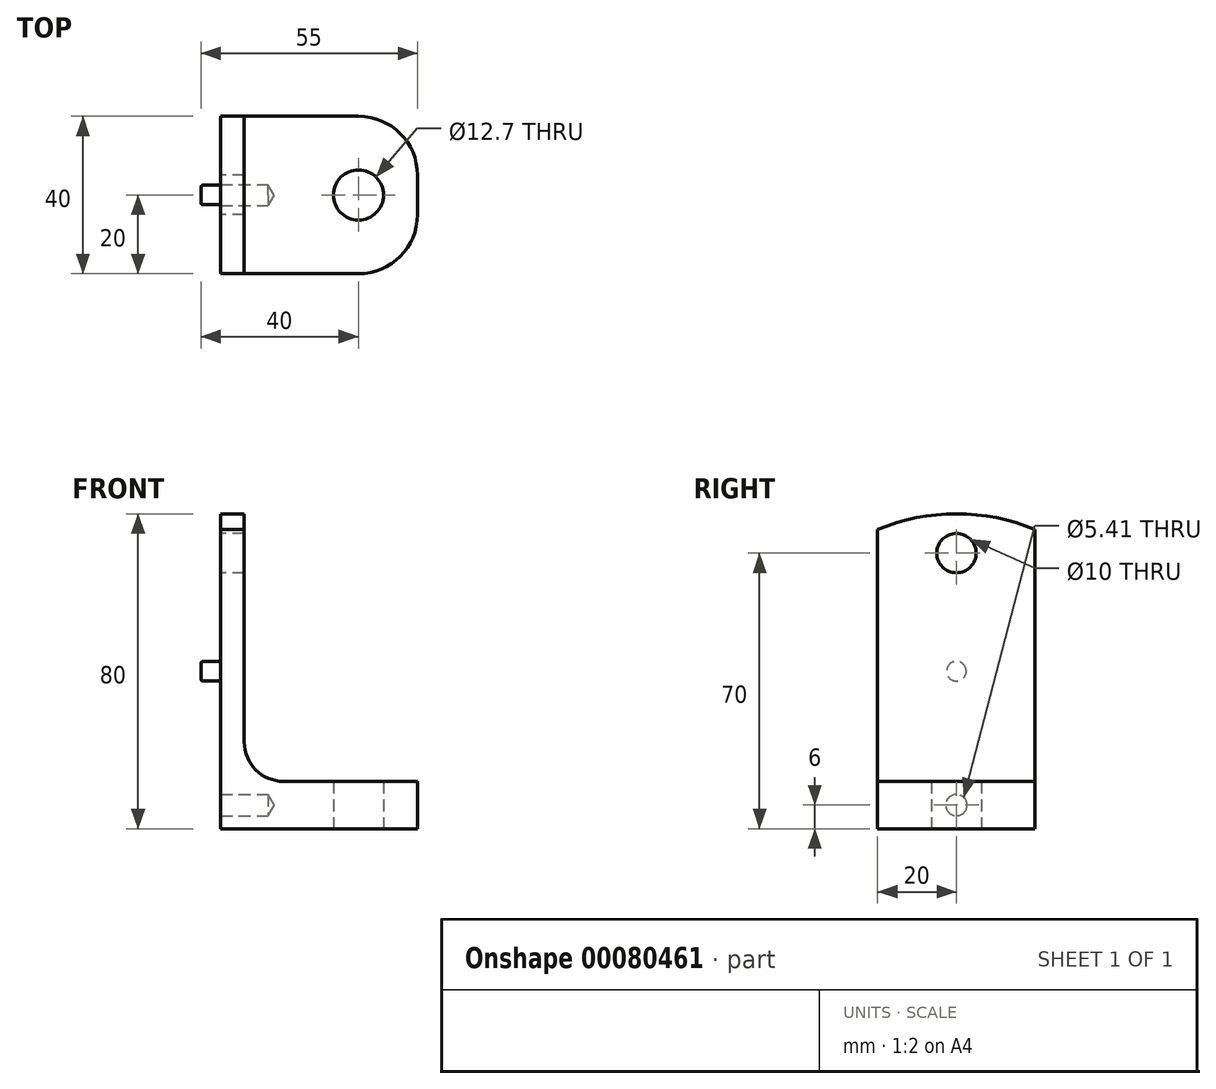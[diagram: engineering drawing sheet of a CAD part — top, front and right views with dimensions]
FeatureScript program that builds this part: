
annotation { "Feature Type Name" : "Feature", "Feature Type Description" : "" }
export const myFeature = defineFeature(function(context is Context, id is Id, definition is map)
    precondition{}
    {
        {
            var Q0;
            Q0=qCreatedBy(makeId("Front.planeOp"),FACE);
            var sketch = newSketch(context, id + "F0", { "sketchPlane" : qUnion([Q0])});
            skLineSegment(sketch, "E0", {"start": v(0, 0) * mm, "end": v(0, 80) * mm});
            skLineSegment(sketch, "E1", {"start": v(0, 80) * mm, "end": v(6, 80) * mm});
            skLineSegment(sketch, "E2", {"start": v(6, 80) * mm, "end": v(6, 12) * mm});
            skLineSegment(sketch, "E3", {"start": v(6, 12) * mm, "end": v(50, 12) * mm});
            skLineSegment(sketch, "E4", {"start": v(50, 12) * mm, "end": v(50, 0) * mm});
            skLineSegment(sketch, "E5", {"start": v(50, 0) * mm, "end": v(0, 0) * mm});
            skSolve(sketch);
        }
        {
            var Q0;
            Q0 = qSketchRegion(id + "F0", true);
            extrude(context, id + "F1", {"entities" : qUnion([Q0]), "depth" : 40 * mm, "symmetric" : true});
        }
        {
            var Q0;
            Q0=makeQuery(id+"F1.opExtrude","SWEPT_EDGE",EDGE,{"disambiguationData":[OSD([sQuery(id+"F0.wireOp",EDGE,"E2"),sQuery(id+"F0.wireOp",EDGE,"E3")])]});
            fillet(context, id + "F2", {"entities" : qUnion([Q0]), "radius" : 10 * mm, "tangentPropagation" : true, "allowEdgeOverflow" : false});
        }
        {
            var Q0;
            Q0=makeQuery(id+"F1.opExtrude","SWEPT_FACE",FACE,{"disambiguationData":[OSD([sQuery(id+"F0.wireOp",EDGE,"E5")])]});
            var sketch = newSketch(context, id + "F3", { "sketchPlane" : qUnion([Q0])});
            skCircle(sketch, "E6", {"center": v(35, 0) * mm, "radius": 6.35 * mm});
            skSolve(sketch);
        }
        {
            var Q0;
            Q0 = qSketchRegion(id + "F3", true);
            extrude(context, id + "F4", {"entities" : qUnion([Q0]), "operationType" : NewBodyOperationType.REMOVE, "endBound" : BoundingType.THROUGH_ALL, "oppositeDirection" : true, "depth" : 25 * mm});
        }
        {
            var Q0;
            Q0=makeQuery(id+"F1.opExtrude","SWEPT_FACE",FACE,{"disambiguationData":[OSD([sQuery(id+"F0.wireOp",EDGE,"E0")])]});
            var sketch = newSketch(context, id + "F5", { "sketchPlane" : qUnion([Q0])});
            skPoint(sketch, "E7", {"position": v(0, 6) * mm});
            skSolve(sketch);
        }
        {
            var Q0;
            Q0=sQuery(id+"F5.wireOp",VERTEX,"E7");
            var Q1;
            Q1=makeQuery(id+"F1.opExtrude","SWEPT_BODY",BODY,{"disambiguationData":[OSD([sQuery(id+"F0.wireOp",EDGE,"E0"),sQuery(id+"F0.wireOp",EDGE,"E1"),sQuery(id+"F0.wireOp",EDGE,"E2"),sQuery(id+"F0.wireOp",EDGE,"E3"),sQuery(id+"F0.wireOp",EDGE,"E4"),sQuery(id+"F0.wireOp",EDGE,"E5")])]});
            hole(context, id + "F6", {"style" : HoleStyle.SIMPLE, "endStyle" : HoleEndStyle.BLIND, "standardTappedOrClearance" : lookupTablePath({ "standard" : "ANSI", "engagement" : "75%", "pitch" : "28 tpi", "size" : "1/4", "type" : "Tapped" }), "standardBlindInLast" : lookupTablePath({ "standard" : "ANSI", "engagement" : "75%", "pitch" : "28 tpi", "size" : "1/4", "type" : "Tapped" }), "holeDiameter" : 5.4 * mm, "holeDepth" : 12 * mm, "locations" : qUnion([Q0]), "scope" : qUnion([Q1]), "majorDiameter" : 6.35 * mm, "startStyle" : HoleStartStyle.PART});
        }
        {
            var Q0;
            Q0=makeQuery(id+"F1.opExtrude","SWEPT_FACE",FACE,{"disambiguationData":[OSD([sQuery(id+"F0.wireOp",EDGE,"E0")])]});
            var sketch = newSketch(context, id + "F7", { "sketchPlane" : qUnion([Q0])});
            skArc(sketch, "E8", {"start": v(20, 76) * mm, "mid": v(0, 80) * mm, "end": v(-20, 76) * mm});
            skLineSegment(sketch, "E9.0", {"start": v(20, 80) * mm, "end": v(-20, 80) * mm});
            skLineSegment(sketch, "E10.0", {"start": v(-20, 76) * mm, "end": v(-20, 80) * mm});
            skLineSegment(sketch, "E10.1", {"start": v(20, 76) * mm, "end": v(20, 80) * mm});
            skPoint(sketch, "E11.orphan", {"position": v(20, 0) * mm});
            skPoint(sketch, "E12.orphan", {"position": v(-20, 0) * mm});
            skCircle(sketch, "E13", {"center": v(0, 70) * mm, "radius": 5 * mm});
            skSolve(sketch);
        }
        {
            var Q0;
            Q0 = qSketchRegion(id + "F7", true);
            extrude(context, id + "F8", {"entities" : qUnion([Q0]), "operationType" : NewBodyOperationType.REMOVE, "endBound" : BoundingType.THROUGH_ALL, "oppositeDirection" : true, "depth" : 25 * mm});
        }
        {
            var Q0;
            Q0=makeQuery(id+"F1.opExtrude","SWEPT_FACE",FACE,{"disambiguationData":[OSD([sQuery(id+"F0.wireOp",EDGE,"E0")])]});
            var sketch = newSketch(context, id + "F9", { "sketchPlane" : qUnion([Q0])});
            skCircle(sketch, "E14", {"center": v(0, 40) * mm, "radius": 2.5 * mm});
            skSolve(sketch);
        }
        {
            var Q0;
            Q0 = qSketchRegion(id + "F9", true);
            extrude(context, id + "F10", {"entities" : qUnion([Q0]), "operationType" : NewBodyOperationType.ADD, "depth" : 5 * mm});
        }
        {
            var Q0;
            Q0=makeQuery(id+"F10.opExtrude","CAP_EDGE",EDGE,{"disambiguationData":[OSD([sQuery(id+"F9.wireOp",EDGE,"E14")])],"isStart":true});
            var Q1;
            Q1=makeQuery(id+"F10.opExtrude","CAP_EDGE",EDGE,{"disambiguationData":[OSD([sQuery(id+"F9.wireOp",EDGE,"E14")])],"isStart":false});
            fillet(context, id + "F11", {"entities" : qUnion([Q0, Q1]), "radius" : 0.5 * mm, "tangentPropagation" : true, "allowEdgeOverflow" : false});
        }
        {
            var Q0;
            Q0=makeQuery(id+"F1.opExtrude","CAP_EDGE",EDGE,{"disambiguationData":[OSD([sQuery(id+"F0.wireOp",EDGE,"E4")])],"isStart":false});
            var Q1;
            Q1=makeQuery(id+"F1.opExtrude","CAP_EDGE",EDGE,{"disambiguationData":[OSD([sQuery(id+"F0.wireOp",EDGE,"E4")])],"isStart":true});
            fillet(context, id + "F12", {"entities" : qUnion([Q0, Q1]), "radius" : 15 * mm, "tangentPropagation" : true, "allowEdgeOverflow" : false});
        }
    });
